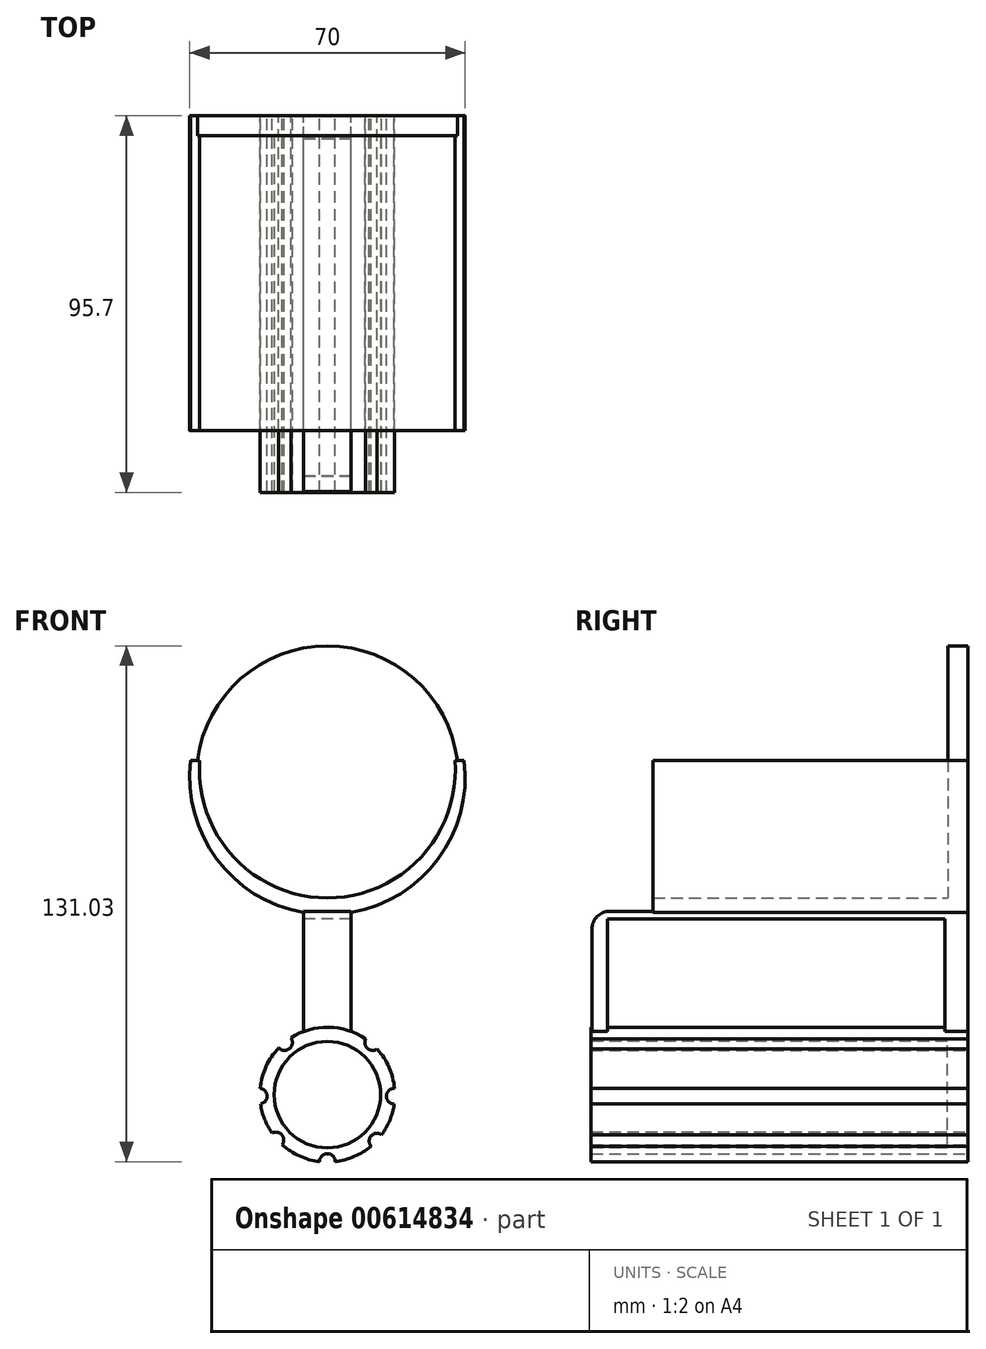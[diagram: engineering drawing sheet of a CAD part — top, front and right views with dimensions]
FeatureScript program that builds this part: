
annotation { "Feature Type Name" : "Feature", "Feature Type Description" : "" }
export const myFeature = defineFeature(function(context is Context, id is Id, definition is map)
    precondition{}
    {
        {
            var Q0;
            Q0=qCreatedBy(makeId("Front.planeOp"),FACE);
            var sketch = newSketch(context, id + "F0", { "sketchPlane" : qUnion([Q0])});
            skCircle(sketch, "E0", {"center": v(0, 0) * mm, "radius": 35 * mm});
            skSolve(sketch);
        }
        {
            var Q0;
            Q0 = qSketchRegion(id + "F0", true);
            var Q1;
            Q1=makeQuery(id+"F0.imprint","IMPRINT",FACE,{"disambiguationData":[TD([[makeQuery(id+"F0.imprint","IMPRINT",EDGE,{"derivedFrom":sQuery(id+"F0.wireOp",EDGE,"E0")}),1.0]])]});
            extrude(context, id + "F1", {"entities" : qUnion([Q0, Q1]), "depth" : 80 * mm, "offsetDistance" : 25 * mm});
        }
        {
            var Q0;
            Q0=qCreatedBy(makeId("Front.planeOp"),FACE);
            var sketch = newSketch(context, id + "F2", { "sketchPlane" : qUnion([Q0])});
            skCircle(sketch, "E1", {"center": v(0, 1.77) * mm, "radius": 32.5 * mm});
            skSolve(sketch);
        }
        {
            var Q0;
            Q0=makeQuery(id+"F2.imprint","IMPRINT",FACE,{"disambiguationData":[TD([[makeQuery(id+"F2.imprint","IMPRINT",EDGE,{"derivedFrom":sQuery(id+"F2.wireOp",EDGE,"E1")}),1.0]])]});
            extrude(context, id + "F3", {"entities" : qUnion([Q0]), "operationType" : NewBodyOperationType.REMOVE, "depth" : 210 * mm, "offsetDistance" : 25 * mm});
        }
        {
            var Q0;
            Q0=qCreatedBy(makeId("Front.planeOp"),FACE);
            var sketch = newSketch(context, id + "F4", { "sketchPlane" : qUnion([Q0])});
            skLineSegment(sketch, "E2", {"start": v(-37.44, 4.21) * mm, "end": v(53.6, 4.21) * mm});
            skLineSegment(sketch, "E3", {"start": v(53.6, 4.21) * mm, "end": v(40.02, 42.94) * mm});
            skLineSegment(sketch, "E4", {"start": v(40.02, 42.94) * mm, "end": v(-37.71, 49.74) * mm});
            skLineSegment(sketch, "E5", {"start": v(-37.71, 49.74) * mm, "end": v(-54.29, 17.53) * mm});
            skLineSegment(sketch, "E6", {"start": v(-54.29, 17.53) * mm, "end": v(-37.44, 4.21) * mm});
            skSolve(sketch);
        }
        {
            var Q0;
            Q0 = qSketchRegion(id + "F4", true);
            extrude(context, id + "F5", {"entities" : qUnion([Q0]), "operationType" : NewBodyOperationType.REMOVE, "depth" : 105.2 * mm, "offsetDistance" : 25 * mm});
        }
        {
            var Q0;
            Q0=qCreatedBy(makeId("Front.planeOp"),FACE);
            var sketch = newSketch(context, id + "F6", { "sketchPlane" : qUnion([Q0])});
            skLineSegment(sketch, "E7.bottom", {"start": v(6.05, -36.01) * mm, "end": v(-6.05, -36.01) * mm});
            skLineSegment(sketch, "E7.top", {"start": v(6.05, -34.1) * mm, "end": v(-6.05, -34.1) * mm});
            skLineSegment(sketch, "E7.left", {"start": v(6.05, -36.01) * mm, "end": v(6.05, -34.1) * mm});
            skLineSegment(sketch, "E7.right", {"start": v(-6.05, -36.01) * mm, "end": v(-6.05, -34.1) * mm});
            skPoint(sketch, "E7.middle", {"position": v(0, -35.06) * mm});
            skSolve(sketch);
        }
        {
            var Q0;
            Q0 = qSketchRegion(id + "F6", true);
            extrude(context, id + "F7", {"entities" : qUnion([Q0]), "operationType" : NewBodyOperationType.ADD, "depth" : 95.5 * mm, "offsetDistance" : 25 * mm});
        }
        {
            var Q0;
            Q0=qCreatedBy(makeId("Front.planeOp"),FACE);
            var sketch = newSketch(context, id + "F8", { "sketchPlane" : qUnion([Q0])});
            skCircle(sketch, "E8", {"center": v(0, 0) * mm, "radius": 33.29 * mm});
            skSolve(sketch);
        }
        {
            var Q0;
            Q0 = qSketchRegion(id + "F8", true);
            extrude(context, id + "F9", {"entities" : qUnion([Q0]), "operationType" : NewBodyOperationType.ADD, "depth" : 5 * mm, "offsetDistance" : 25 * mm});
        }
        {
            var Q0;
            Q0=makeQuery(id+"F7.opExtrude","SWEPT_FACE",FACE,{"disambiguationData":[OSD([sQuery(id+"F6.wireOp",EDGE,"E7.bottom")])]});
            var sketch = newSketch(context, id + "F10", { "sketchPlane" : qUnion([Q0])});
            skLineSegment(sketch, "E9.bottom", {"start": v(6.05, 95.5) * mm, "end": v(-6.05, 95.5) * mm});
            skLineSegment(sketch, "E9.top", {"start": v(6.05, 91.51) * mm, "end": v(-6.05, 91.51) * mm});
            skLineSegment(sketch, "E9.left", {"start": v(6.05, 95.5) * mm, "end": v(6.05, 91.51) * mm});
            skLineSegment(sketch, "E9.right", {"start": v(-6.05, 95.5) * mm, "end": v(-6.05, 91.51) * mm});
            skPoint(sketch, "E9.middle", {"position": v(0, 93.5) * mm});
            skPoint(sketch, "E9.middle.positionSnap0", {"position": v(0, 95.5) * mm});
            skPoint(sketch, "E9.centerSnap0", {"position": v(0, 95.5) * mm});
            skSolve(sketch);
        }
        {
            var Q0;
            Q0 = qSketchRegion(id + "F10", true);
            extrude(context, id + "F11", {"entities" : qUnion([Q0]), "operationType" : NewBodyOperationType.ADD, "depth" : 40 * mm, "offsetDistance" : 25 * mm});
        }
        {
            var Q0;
            Q0=makeQuery(id+"F7.opExtrude","CAP_EDGE",EDGE,{"disambiguationData":[OSD([sQuery(id+"F6.wireOp",EDGE,"E7.top")])],"isStart":false});
            fillet(context, id + "F12", {"entities" : qUnion([Q0]), "radius" : 4.6 * mm, "tangentPropagation" : true, "allowEdgeOverflow" : false});
        }
        {
            var Q0;
            Q0=qCreatedBy(makeId("Front.planeOp"),FACE);
            var sketch = newSketch(context, id + "F13", { "sketchPlane" : qUnion([Q0])});
            skCircle(sketch, "E10", {"center": v(0, -80.72) * mm, "radius": 17.13 * mm});
            skSolve(sketch);
        }
        {
            var Q0;
            Q0 = qSketchRegion(id + "F13", true);
            extrude(context, id + "F14", {"entities" : qUnion([Q0]), "operationType" : NewBodyOperationType.ADD, "depth" : 95.7 * mm, "offsetDistance" : 25 * mm});
        }
        {
            var Q0;
            Q0=makeQuery(id+"F7.opExtrude","SWEPT_FACE",FACE,{"disambiguationData":[OSD([sQuery(id+"F6.wireOp",EDGE,"E7.bottom")])]});
            var sketch = newSketch(context, id + "F15", { "sketchPlane" : qUnion([Q0])});
            skLineSegment(sketch, "E11.bottom", {"start": v(6.05, 0) * mm, "end": v(-6.05, 0) * mm});
            skLineSegment(sketch, "E11.top", {"start": v(6.05, 5.8) * mm, "end": v(-6.05, 5.8) * mm});
            skLineSegment(sketch, "E11.left", {"start": v(6.05, 0) * mm, "end": v(6.05, 5.8) * mm});
            skLineSegment(sketch, "E11.right", {"start": v(-6.05, 0) * mm, "end": v(-6.05, 5.8) * mm});
            skPoint(sketch, "E11.middle", {"position": v(0, 2.9) * mm});
            skSolve(sketch);
        }
        {
            var Q0;
            Q0 = qSketchRegion(id + "F15", true);
            extrude(context, id + "F16", {"entities" : qUnion([Q0]), "operationType" : NewBodyOperationType.ADD, "depth" : 43.3 * mm, "offsetDistance" : 25 * mm});
        }
        {
            var Q0;
            Q0=qCreatedBy(makeId("Front.planeOp"),FACE);
            var sketch = newSketch(context, id + "F17", { "sketchPlane" : qUnion([Q0])});
            skCircle(sketch, "E12", {"center": v(-17.3, -81.11) * mm, "radius": 2 * mm});
            skCircle(sketch, "E13", {"center": v(17, -81.11) * mm, "radius": 2 * mm});
            skCircle(sketch, "E14", {"center": v(0, -97.71) * mm, "radius": 2 * mm});
            skCircle(sketch, "E15", {"center": v(-13.08, -92.23) * mm, "radius": 2 * mm});
            skCircle(sketch, "E16", {"center": v(12.6, -92.54) * mm, "radius": 2 * mm});
            skCircle(sketch, "E17", {"center": v(11.5, -67.49) * mm, "radius": 2 * mm});
            skCircle(sketch, "E18", {"center": v(-10.88, -67.49) * mm, "radius": 2 * mm});
            skSolve(sketch);
        }
        {
            var Q0;
            Q0 = qSketchRegion(id + "F17", true);
            extrude(context, id + "F18", {"entities" : qUnion([Q0]), "operationType" : NewBodyOperationType.REMOVE, "depth" : 126 * mm, "offsetDistance" : 25 * mm});
        }
        {
            var Q0;
            Q0=makeQuery(id+"F14.opExtrude","CAP_FACE",FACE,{"disambiguationData":[OSD([sQuery(id+"F13.wireOp",EDGE,"E10")])],"isStart":false});
            var sketch = newSketch(context, id + "F19", { "sketchPlane" : qUnion([Q0])});
            skCircle(sketch, "E19", {"center": v(0, -80.72) * mm, "radius": 13.52 * mm});
            skSolve(sketch);
        }
        {
            var Q0;
            Q0 = qSketchRegion(id + "F19", true);
            extrude(context, id + "F20", {"entities" : qUnion([Q0]), "operationType" : NewBodyOperationType.REMOVE, "oppositeDirection" : true, "depth" : 90.5 * mm, "offsetDistance" : 25 * mm});
        }
    });
